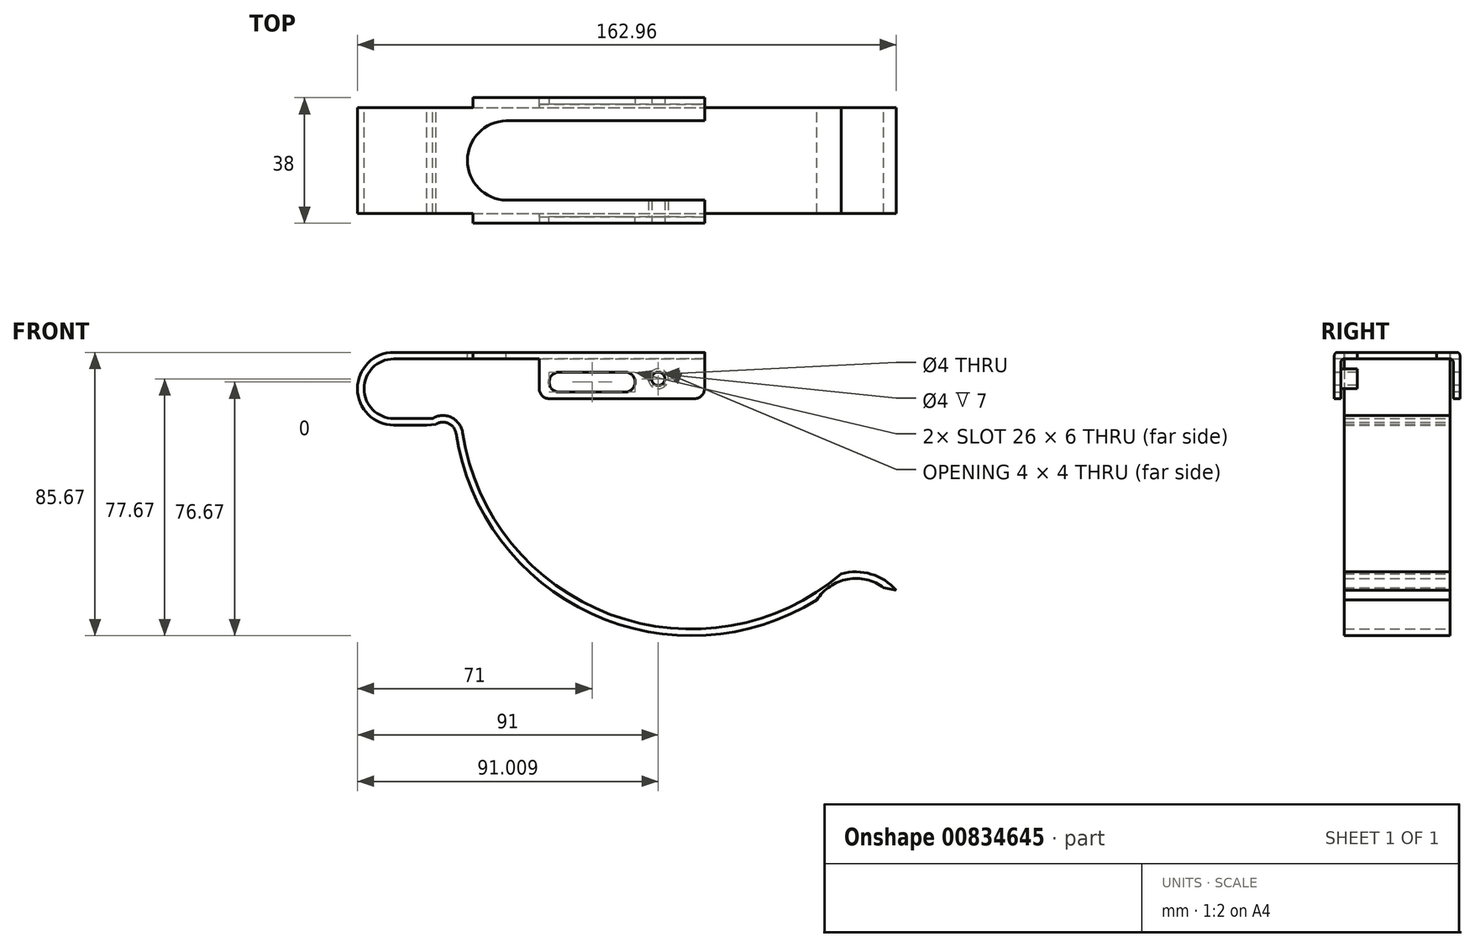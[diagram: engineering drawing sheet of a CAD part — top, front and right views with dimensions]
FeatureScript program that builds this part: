
annotation { "Feature Type Name" : "Feature", "Feature Type Description" : "" }
export const myFeature = defineFeature(function(context is Context, id is Id, definition is map)
    precondition{}
    {
        {
            var Q0;
            Q0=qCreatedBy(makeId("Front.planeOp"),FACE);
            var sketch = newSketch(context, id + "F0", { "sketchPlane" : qUnion([Q0])});
            skArc(sketch, "E0", {"start": v(0, 11) * mm, "mid": v(-11, 0) * mm, "end": v(0, -11) * mm});
            skLineSegment(sketch, "E1", {"start": v(0, 11) * mm, "end": v(94, 11) * mm});
            skLineSegment(sketch, "E2", {"start": v(0, -11) * mm, "end": v(10, -11) * mm});
            skArc(sketch, "E3", {"start": v(18.82, -13.5) * mm, "mid": v(59.85, -68.06) * mm, "end": v(127.97, -63.84) * mm});
            skArc(sketch, "E4", {"start": v(148.2, -60.2) * mm, "mid": v(137.3, -57.6) * mm, "end": v(127.97, -63.84) * mm});
            skPoint(sketch, "E5.visualSharp", {"position": v(18.48, -11) * mm});
            skArc(sketch, "E5.filletArc", {"start": v(18.82, -13.5) * mm, "mid": v(16.53, -10.48) * mm, "end": v(12.74, -10.72) * mm});
            skLineSegment(sketch, "E6.0", {"start": v(0, 9) * mm, "end": v(94, 9) * mm});
            skArc(sketch, "E6.1", {"start": v(0, 9) * mm, "mid": v(-9, 0) * mm, "end": v(0, -9) * mm});
            skArc(sketch, "E6.2", {"start": v(151.96, -61) * mm, "mid": v(144.39, -56.05) * mm, "end": v(135.34, -56) * mm});
            skArc(sketch, "E6.3", {"start": v(20.8, -13.2) * mm, "mid": v(65.5, -68.25) * mm, "end": v(135.34, -56) * mm});
            skArc(sketch, "E6.4", {"start": v(20.8, -13.2) * mm, "mid": v(17.4, -8.67) * mm, "end": v(11.72, -9) * mm});
            skLineSegment(sketch, "E6.5", {"start": v(0, -9) * mm, "end": v(11.72, -9) * mm});
            skLineSegment(sketch, "E7", {"start": v(94, 11) * mm, "end": v(94, 9) * mm});
            skLineSegment(sketch, "E8", {"start": v(148.2, -60.2) * mm, "end": v(151.96, -61) * mm});
            skLineSegment(sketch, "E9", {"start": v(12.74, -10.72) * mm, "end": v(10, -11) * mm});
            skSolve(sketch);
        }
        {
            var Q0;
            Q0=makeQuery(id+"F0.imprint","IMPRINT",FACE,{"disambiguationData":[TD([[makeQuery(id+"F0.imprint","IMPRINT",EDGE,{"derivedFrom":sQuery(id+"F0.wireOp",EDGE,"E0")}),1.0]])]});
            extrude(context, id + "F1", {"entities" : qUnion([Q0]), "depth" : 16 * mm, "offsetDistance" : 25 * mm});
        }
        {
            var Q0;
            Q0=makeQuery(id+"F1.opExtrude","SWEPT_FACE",FACE,{"disambiguationData":[OSD([sQuery(id+"F0.wireOp",EDGE,"E1")])]});
            var sketch = newSketch(context, id + "F2", { "sketchPlane" : qUnion([Q0])});
            skSolve(sketch);
        }
        {
            var Q0;
            {var subQ0=sQuery(id+"F0.wireOp",EDGE,"E1");Q0=makeQuery(id+"F2.imprint","IMPRINT",FACE,{"disambiguationData":[TD([[makeQuery(id+"F2.imprint","IMPRINT",EDGE,{"derivedFrom":makeQuery(id+"F1.opExtrude","CAP_EDGE",EDGE,{"disambiguationData":[OSD([subQ0])],"isStart":true})}),-1.0]])]});}
            var sketch = newSketch(context, id + "F3", { "sketchPlane" : qUnion([Q0])});
            skLineSegment(sketch, "E10.bottom", {"start": v(94, -16) * mm, "end": v(24, -16) * mm});
            skLineSegment(sketch, "E10.top", {"start": v(94, -19) * mm, "end": v(24, -19) * mm});
            skLineSegment(sketch, "E10.left", {"start": v(94, -16) * mm, "end": v(94, -19) * mm});
            skLineSegment(sketch, "E10.right", {"start": v(24, -16) * mm, "end": v(24, -19) * mm});
            skSolve(sketch);
        }
        {
            var Q0;
            Q0=makeQuery(id+"F3.imprint","IMPRINT",FACE,{"disambiguationData":[TD([[makeQuery(id+"F3.imprint","IMPRINT",EDGE,{"derivedFrom":sQuery(id+"F3.wireOp",EDGE,"E10.bottom")}),-1.0]])]});
            extrude(context, id + "F4", {"entities" : qUnion([Q0]), "operationType" : NewBodyOperationType.ADD, "oppositeDirection" : true, "depth" : 2 * mm, "offsetDistance" : 25 * mm});
        }
        {
            var Q0;
            Q0=makeQuery(id+"F4.opExtrude","SWEPT_FACE",FACE,{"disambiguationData":[OSD([sQuery(id+"F3.wireOp",EDGE,"E10.top")])]});
            var sketch = newSketch(context, id + "F5", { "sketchPlane" : qUnion([Q0])});
            skLineSegment(sketch, "E11.bottom", {"start": v(94, 11) * mm, "end": v(44, 11) * mm});
            skLineSegment(sketch, "E11.top", {"start": v(94, -3) * mm, "end": v(44, -3) * mm});
            skLineSegment(sketch, "E11.left", {"start": v(94, 11) * mm, "end": v(94, -3) * mm});
            skLineSegment(sketch, "E11.right", {"start": v(44, 11) * mm, "end": v(44, -3) * mm});
            skSolve(sketch);
        }
        {
            var Q0;
            {var subQ0=sQuery(id+"F5.wireOp",EDGE,"E11.top");Q0=makeQuery(id+"F5.imprint","IMPRINT",FACE,{"disambiguationData":[TD([[makeQuery(id+"F5.imprint","IMPRINT",EDGE,{"derivedFrom":subQ0}),-1.0]])]});}
            var Q1;
            {var subQ0=sQuery(id+"F5.wireOp",EDGE,"E11.bottom");Q1=makeQuery(id+"F5.imprint","IMPRINT",FACE,{"disambiguationData":[TD([[makeQuery(id+"F5.imprint","IMPRINT",EDGE,{"derivedFrom":subQ0}),1.0]])]});}
            extrude(context, id + "F6", {"entities" : qUnion([Q0, Q1]), "operationType" : NewBodyOperationType.ADD, "oppositeDirection" : true, "depth" : 2 * mm, "offsetDistance" : 25 * mm});
        }
        {
            var Q0;
            Q0=makeQuery(id+"F4.opExtrude","CAP_EDGE",EDGE,{"disambiguationData":[OSD([sQuery(id+"F3.wireOp",EDGE,"E10.top")])],"isStart":true});
            var Q1;
            Q1=makeQuery(id+"F6.boolean.opBoolean","INTERSECT",EDGE,{"derivedFrom":[makeQuery(id+"F4.boolean.opBoolean","MERGE",FACE,{"derivedFrom":[makeQuery(id+"F1.opExtrude","SWEPT_FACE",FACE,{"disambiguationData":[OSD([sQuery(id+"F0.wireOp",EDGE,"E6.0")])]}),makeQuery(id+"F4.opExtrude","CAP_FACE",FACE,{"disambiguationData":[OSD([sQuery(id+"F3.wireOp",EDGE,"E10.bottom"),sQuery(id+"F3.wireOp",EDGE,"E10.top"),sQuery(id+"F3.wireOp",EDGE,"E10.left"),sQuery(id+"F3.wireOp",EDGE,"E10.right")])],"isStart":false})]}),makeQuery(id+"F6.opExtrude","CAP_FACE",FACE,{"disambiguationData":[OSD([sQuery(id+"F5.wireOp",EDGE,"E11.bottom"),sQuery(id+"F5.wireOp",EDGE,"E11.top"),sQuery(id+"F5.wireOp",EDGE,"E11.left"),sQuery(id+"F5.wireOp",EDGE,"E11.right")])],"isStart":false})]});
            fillet(context, id + "F7", {"entities" : qUnion([Q0, Q1]), "radius" : 1 * mm, "tangentPropagation" : true, "allowEdgeOverflow" : false});
        }
        {
            var Q0;
            Q0=makeQuery(id+"F1.opExtrude","SWEPT_BODY",BODY,{"disambiguationData":[OSD([sQuery(id+"F0.wireOp",EDGE,"E0"),sQuery(id+"F0.wireOp",EDGE,"E1"),sQuery(id+"F0.wireOp",EDGE,"E2"),sQuery(id+"F0.wireOp",EDGE,"E3"),sQuery(id+"F0.wireOp",EDGE,"E4"),sQuery(id+"F0.wireOp",EDGE,"E5.filletArc"),sQuery(id+"F0.wireOp",EDGE,"E6.0"),sQuery(id+"F0.wireOp",EDGE,"E6.1"),sQuery(id+"F0.wireOp",EDGE,"E6.2"),sQuery(id+"F0.wireOp",EDGE,"E6.3"),sQuery(id+"F0.wireOp",EDGE,"E6.4"),sQuery(id+"F0.wireOp",EDGE,"E6.5"),sQuery(id+"F0.wireOp",EDGE,"E7"),sQuery(id+"F0.wireOp",EDGE,"E8"),sQuery(id+"F0.wireOp",EDGE,"E9")])]});
            var Q1;
            Q1=qCreatedBy(makeId("Front.planeOp"),FACE);
            mirror(context, id + "F8", {"operationType" : NewBodyOperationType.ADD, "entities" : qUnion([Q0]), "mirrorPlane" : qUnion([Q1])});
        }
        {
            var Q0;
            {var subQ0=sQuery(id+"F0.wireOp",EDGE,"E1");Q0=makeQuery(id+"F2.imprint","IMPRINT",FACE,{"disambiguationData":[TD([[makeQuery(id+"F2.imprint","IMPRINT",EDGE,{"derivedFrom":makeQuery(id+"F1.opExtrude","CAP_EDGE",EDGE,{"disambiguationData":[OSD([subQ0])],"isStart":true})}),-1.0]])]});}
            var sketch = newSketch(context, id + "F9", { "sketchPlane" : qUnion([Q0])});
            skLineSegment(sketch, "E12", {"start": v(94, -12) * mm, "end": v(34, -12) * mm});
            skLineSegment(sketch, "E13", {"start": v(94, 12) * mm, "end": v(34, 12) * mm});
            skArc(sketch, "E14", {"start": v(34, 12) * mm, "mid": v(22.27, 0) * mm, "end": v(34, -12) * mm});
            skPoint(sketch, "E14.third.point", {"position": v(22.74, -3.3) * mm});
            skLineSegment(sketch, "E15", {"start": v(94, -12) * mm, "end": v(94, 12) * mm});
            skPoint(sketch, "E16.orphan", {"position": v(34, 12) * mm});
            skSolve(sketch);
        }
        {
            var Q0;
            {var subQ0=sQuery(id+"F9.wireOp",EDGE,"E12");Q0=makeQuery(id+"F9.imprint","IMPRINT",FACE,{"disambiguationData":[TD([[makeQuery(id+"F9.imprint","IMPRINT",EDGE,{"derivedFrom":subQ0}),-1.0]])]});}
            var Q1;
            {var subQ0=sQuery(id+"F9.wireOp",EDGE,"E13");Q1=makeQuery(id+"F9.imprint","IMPRINT",FACE,{"disambiguationData":[TD([[makeQuery(id+"F9.imprint","IMPRINT",EDGE,{"derivedFrom":subQ0}),1.0]])]});}
            extrude(context, id + "F10", {"entities" : qUnion([Q0, Q1]), "operationType" : NewBodyOperationType.REMOVE, "oppositeDirection" : true, "depth" : 2 * mm, "offsetDistance" : 25 * mm});
        }
        {
            var Q0;
            Q0=qCreatedBy(makeId("Front.planeOp"),FACE);
            var sketch = newSketch(context, id + "F11", { "sketchPlane" : qUnion([Q0])});
            skLineSegment(sketch, "E17", {"start": v(50, 2) * mm, "end": v(70, 2) * mm});
            skArc(sketch, "E18.0.startCap", {"start": v(50, -1) * mm, "mid": v(47, 2) * mm, "end": v(50, 5) * mm});
            skArc(sketch, "E18.0.endCap", {"start": v(70, 5) * mm, "mid": v(73, 2) * mm, "end": v(70, -1) * mm});
            skLineSegment(sketch, "E18.0.left", {"start": v(50, 5) * mm, "end": v(70, 5) * mm});
            skLineSegment(sketch, "E18.0.right", {"start": v(50, -1) * mm, "end": v(70, -1) * mm});
            skSolve(sketch);
        }
        {
            var Q0;
            Q0 = qSketchRegion(id + "F11", true);
            extrude(context, id + "F12", {"entities" : qUnion([Q0]), "operationType" : NewBodyOperationType.REMOVE, "depth" : 25 * mm, "offsetDistance" : 25 * mm});
        }
        {
            var Q0;
            Q0 = qSketchRegion(id + "F11", true);
            extrude(context, id + "F13", {"entities" : qUnion([Q0]), "operationType" : NewBodyOperationType.REMOVE, "oppositeDirection" : true, "depth" : 25 * mm, "offsetDistance" : 25 * mm});
        }
        {
            var Q0;
            Q0=qCreatedBy(makeId("Front.planeOp"),FACE);
            var sketch = newSketch(context, id + "F14", { "sketchPlane" : qUnion([Q0])});
            skPoint(sketch, "E19", {"position": v(80, 3) * mm});
            skSolve(sketch);
        }
        {
            var Q0;
            Q0=sQuery(id+"F14.wireOp",VERTEX,"E19");
            var Q1;
            Q1=makeQuery(id+"F1.opExtrude","SWEPT_BODY",BODY,{"disambiguationData":[OSD([sQuery(id+"F0.wireOp",EDGE,"E0"),sQuery(id+"F0.wireOp",EDGE,"E1"),sQuery(id+"F0.wireOp",EDGE,"E2"),sQuery(id+"F0.wireOp",EDGE,"E3"),sQuery(id+"F0.wireOp",EDGE,"E4"),sQuery(id+"F0.wireOp",EDGE,"E5.filletArc"),sQuery(id+"F0.wireOp",EDGE,"E6.0"),sQuery(id+"F0.wireOp",EDGE,"E6.1"),sQuery(id+"F0.wireOp",EDGE,"E6.2"),sQuery(id+"F0.wireOp",EDGE,"E6.3"),sQuery(id+"F0.wireOp",EDGE,"E6.4"),sQuery(id+"F0.wireOp",EDGE,"E6.5"),sQuery(id+"F0.wireOp",EDGE,"E7"),sQuery(id+"F0.wireOp",EDGE,"E8"),sQuery(id+"F0.wireOp",EDGE,"E9")])]});
            hole(context, id + "F15", {"style" : HoleStyle.SIMPLE, "endStyle" : HoleEndStyle.THROUGH, "holeDiameter" : 4 * mm, "majorDiameter" : 5 * mm, "isTappedThrough" : true, "tappedDepth" : 12 * mm, "tapClearance" : 3, "locations" : qUnion([Q0]), "scope" : qUnion([Q1])});
        }
        {
            var Q0;
            Q0=makeQuery(id+"F6.boolean.opBoolean","MERGE",FACE,{"derivedFrom":[makeQuery(id+"F4.opExtrude","SWEPT_FACE",FACE,{"disambiguationData":[OSD([sQuery(id+"F3.wireOp",EDGE,"E10.top")])]}),makeQuery(id+"F6.opExtrude","CAP_FACE",FACE,{"disambiguationData":[OSD([sQuery(id+"F5.wireOp",EDGE,"E11.bottom"),sQuery(id+"F5.wireOp",EDGE,"E11.top"),sQuery(id+"F5.wireOp",EDGE,"E11.left"),sQuery(id+"F5.wireOp",EDGE,"E11.right")])],"isStart":true})]});
            var sketch = newSketch(context, id + "F16", { "sketchPlane" : qUnion([Q0])});
            skPoint(sketch, "E20", {"position": v(80, 3) * mm});
            skSolve(sketch);
        }
        {
            var Q0;
            Q0=sQuery(id+"F16.wireOp",VERTEX,"E20");
            var Q1;
            Q1=makeQuery(id+"F1.opExtrude","SWEPT_BODY",BODY,{"disambiguationData":[OSD([sQuery(id+"F0.wireOp",EDGE,"E0"),sQuery(id+"F0.wireOp",EDGE,"E1"),sQuery(id+"F0.wireOp",EDGE,"E2"),sQuery(id+"F0.wireOp",EDGE,"E3"),sQuery(id+"F0.wireOp",EDGE,"E4"),sQuery(id+"F0.wireOp",EDGE,"E5.filletArc"),sQuery(id+"F0.wireOp",EDGE,"E6.0"),sQuery(id+"F0.wireOp",EDGE,"E6.1"),sQuery(id+"F0.wireOp",EDGE,"E6.2"),sQuery(id+"F0.wireOp",EDGE,"E6.3"),sQuery(id+"F0.wireOp",EDGE,"E6.4"),sQuery(id+"F0.wireOp",EDGE,"E6.5"),sQuery(id+"F0.wireOp",EDGE,"E7"),sQuery(id+"F0.wireOp",EDGE,"E8"),sQuery(id+"F0.wireOp",EDGE,"E9")])]});
            hole(context, id + "F17", {"style" : HoleStyle.SIMPLE, "endStyle" : HoleEndStyle.THROUGH, "holeDiameter" : 4 * mm, "majorDiameter" : 5 * mm, "isTappedThrough" : true, "tappedDepth" : 12 * mm, "tapClearance" : 3, "locations" : qUnion([Q0]), "scope" : qUnion([Q1])});
        }
        {
            var Q0;
            Q0=makeQuery(id+"F6.opExtrude","CAP_FACE",FACE,{"disambiguationData":[OSD([sQuery(id+"F5.wireOp",EDGE,"E11.bottom"),sQuery(id+"F5.wireOp",EDGE,"E11.top"),sQuery(id+"F5.wireOp",EDGE,"E11.left"),sQuery(id+"F5.wireOp",EDGE,"E11.right")])],"isStart":false});
            var sketch = newSketch(context, id + "F18", { "sketchPlane" : qUnion([Q0])});
            skLineSegment(sketch, "E21.0.0", {"start": v(-44, -3) * mm, "end": v(-44, 8) * mm});
            skLineSegment(sketch, "E21.0.1", {"start": v(-44, 8) * mm, "end": v(-94, 8) * mm});
            skLineSegment(sketch, "E21.0.2", {"start": v(-94, 8) * mm, "end": v(-94, -3) * mm});
            skLineSegment(sketch, "E21.0.3", {"start": v(-94, -3) * mm, "end": v(-44, -3) * mm});
            skCircle(sketch, "E22.0", {"center": v(-80, 3) * mm, "radius": 3 * mm});
            skSolve(sketch);
        }
        {
            var Q0;
            Q0=makeQuery(id+"F18.imprint","IMPRINT",FACE,{"disambiguationData":[TD([[makeQuery(id+"F18.imprint","IMPRINT",EDGE,{"derivedFrom":sQuery(id+"F18.wireOp",EDGE,"E22.0")}),1.0]])]});
            extrude(context, id + "F19", {"entities" : qUnion([Q0]), "operationType" : NewBodyOperationType.ADD, "depth" : 5 * mm, "offsetDistance" : 25 * mm});
        }
        {
            var Q0;
            Q0=makeQuery(id+"F8.opPattern","COPY",EDGE,{"derivedFrom":makeQuery(id+"F6.opExtrude","SWEPT_EDGE",EDGE,{"disambiguationData":[OSD([sQuery(id+"F5.wireOp",EDGE,"E11.top"),sQuery(id+"F5.wireOp",EDGE,"E11.right")])]}),"instanceName":"1"});
            var Q1;
            Q1=makeQuery(id+"F6.opExtrude","SWEPT_EDGE",EDGE,{"disambiguationData":[OSD([sQuery(id+"F5.wireOp",EDGE,"E11.top"),sQuery(id+"F5.wireOp",EDGE,"E11.right")])]});
            var Q2;
            Q2=makeQuery(id+"F6.opExtrude","SWEPT_EDGE",EDGE,{"disambiguationData":[OSD([sQuery(id+"F5.wireOp",EDGE,"E11.top"),sQuery(id+"F5.wireOp",EDGE,"E11.left")])]});
            var Q3;
            Q3=makeQuery(id+"F8.opPattern","COPY",EDGE,{"derivedFrom":makeQuery(id+"F6.opExtrude","SWEPT_EDGE",EDGE,{"disambiguationData":[OSD([sQuery(id+"F5.wireOp",EDGE,"E11.top"),sQuery(id+"F5.wireOp",EDGE,"E11.left")])]}),"instanceName":"1"});
            fillet(context, id + "F20", {"entities" : qUnion([Q0, Q1, Q2, Q3]), "radius" : 3 * mm, "tangentPropagation" : true, "allowEdgeOverflow" : false});
        }
    });
